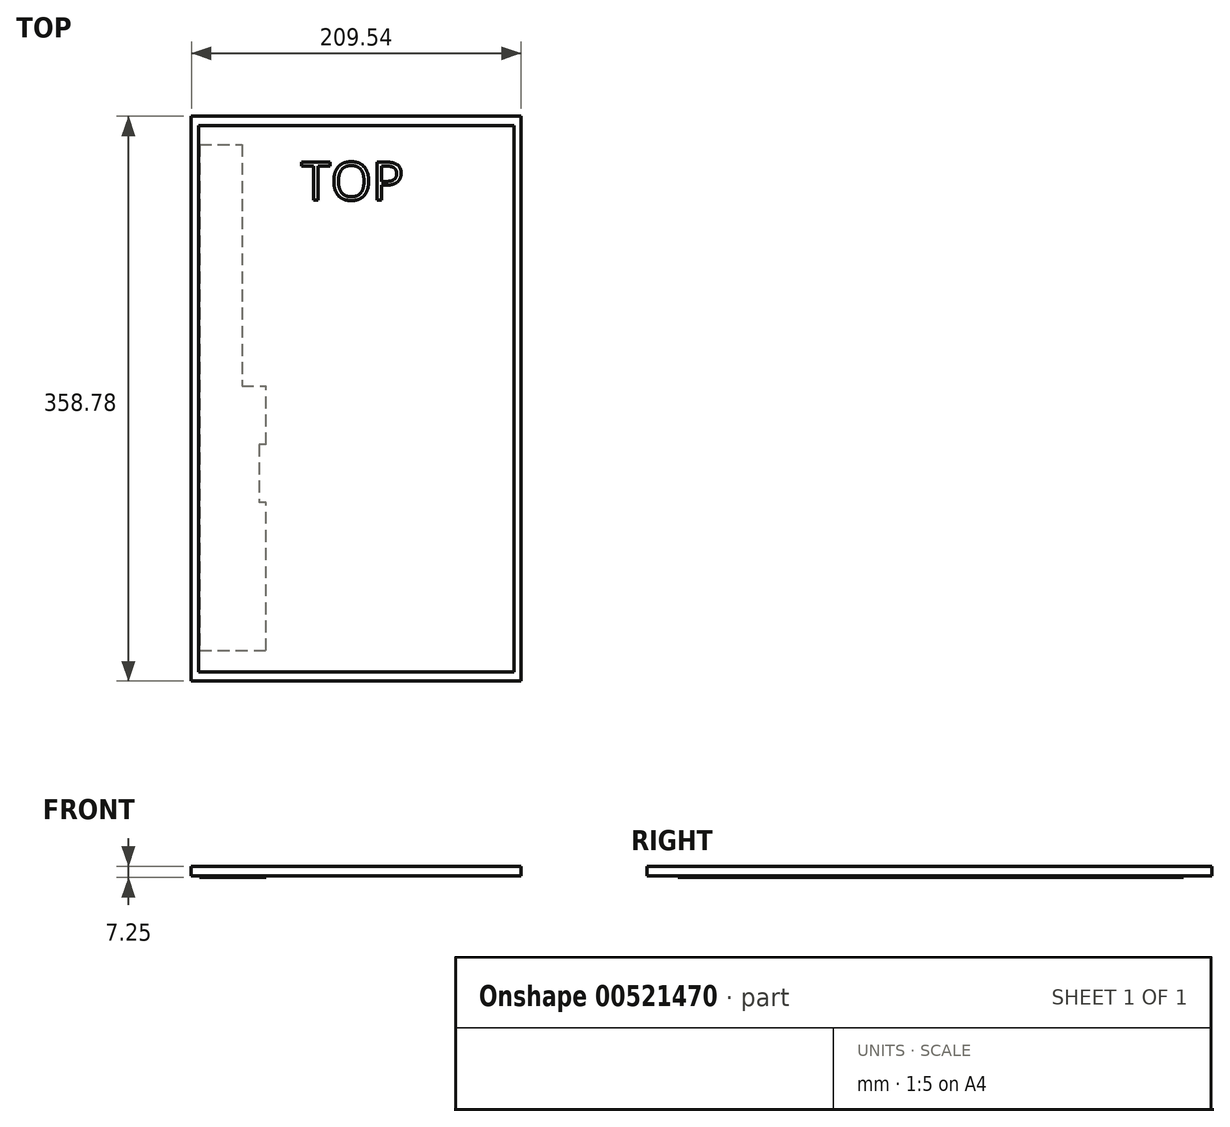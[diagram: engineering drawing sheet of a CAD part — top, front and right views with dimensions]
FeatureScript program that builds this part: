
annotation { "Feature Type Name" : "Feature", "Feature Type Description" : "" }
export const myFeature = defineFeature(function(context is Context, id is Id, definition is map)
    precondition{}
    {
        {
            var Q0;
            Q0=qCreatedBy(makeId("Top.planeOp"),FACE);
            var sketch = newSketch(context, id + "F0", { "sketchPlane" : qUnion([Q0])});
            skLineSegment(sketch, "E0.bottom", {"start": v(-104.77, 179.39) * mm, "end": v(104.78, 179.39) * mm});
            skLineSegment(sketch, "E0.top", {"start": v(-104.78, -179.39) * mm, "end": v(104.77, -179.39) * mm});
            skLineSegment(sketch, "E0.left", {"start": v(-104.77, 179.39) * mm, "end": v(-104.78, -179.39) * mm});
            skLineSegment(sketch, "E0.right", {"start": v(104.78, 179.39) * mm, "end": v(104.77, -179.39) * mm});
            skPoint(sketch, "E0.middle", {"position": v(0, 0) * mm});
            skSolve(sketch);
        }
        {
            var Q0;
            Q0=makeQuery(id+"F0.imprint","IMPRINT",FACE,{"disambiguationData":[TD([[makeQuery(id+"F0.imprint","IMPRINT",EDGE,{"derivedFrom":sQuery(id+"F0.wireOp",EDGE,"E0.bottom")}),-1.0]])]});
            extrude(context, id + "F1", {"entities" : qUnion([Q0]), "depth" : 6 * mm, "offsetDistance" : 25 * mm});
        }
        {
            var Q0;
            Q0=makeQuery(id+"F1.opExtrude","CAP_FACE",FACE,{"disambiguationData":[OSD([sQuery(id+"F0.wireOp",EDGE,"E0.bottom"),sQuery(id+"F0.wireOp",EDGE,"E0.top"),sQuery(id+"F0.wireOp",EDGE,"E0.left"),sQuery(id+"F0.wireOp",EDGE,"E0.right")])],"isStart":false});
            var sketch = newSketch(context, id + "F2", { "sketchPlane" : qUnion([Q0])});
            skLineSegment(sketch, "E1.bottom", {"start": v(-100.08, 173.39) * mm, "end": v(100.08, 173.39) * mm});
            skLineSegment(sketch, "E1.top", {"start": v(-100.08, -173.39) * mm, "end": v(100.08, -173.39) * mm});
            skLineSegment(sketch, "E1.left", {"start": v(-100.08, 173.39) * mm, "end": v(-100.08, -173.39) * mm});
            skLineSegment(sketch, "E1.right", {"start": v(100.08, 173.39) * mm, "end": v(100.08, -173.39) * mm});
            skPoint(sketch, "E1.middle", {"position": v(0, 0) * mm});
            skSolve(sketch);
        }
        {
            var Q0;
            Q0=makeQuery(id+"F2.imprint","IMPRINT",FACE,{"disambiguationData":[TD([[makeQuery(id+"F2.imprint","IMPRINT",EDGE,{"derivedFrom":sQuery(id+"F2.wireOp",EDGE,"E1.bottom")}),-1.0]])]});
            extrude(context, id + "F3", {"entities" : qUnion([Q0]), "operationType" : NewBodyOperationType.REMOVE, "oppositeDirection" : true, "depth" : 0.25 * mm, "offsetDistance" : 25 * mm});
        }
        {
            var Q0;
            Q0=makeQuery(id+"F3.boolean.opBoolean","COPY",FACE,{"derivedFrom":makeQuery(id+"F3.opExtrude","CAP_FACE",FACE,{"disambiguationData":[OSD([sQuery(id+"F2.wireOp",EDGE,"E1.bottom"),sQuery(id+"F2.wireOp",EDGE,"E1.top"),sQuery(id+"F2.wireOp",EDGE,"E1.left"),sQuery(id+"F2.wireOp",EDGE,"E1.right")])],"isStart":false})});
            var sketch = newSketch(context, id + "F4", { "sketchPlane" : qUnion([Q0])});
            skText(sketch, "E2", { "text": "TOP", "fontName": "OpenSans-Regular.ttf"});
            const initialGuessF4  = {"E2": [-0.03496, 0.12616, 1, 0, 0.02427]};
            skSetInitialGuess(sketch, initialGuessF4);
            skSolve(sketch);
        }
        {
            var Q0;
            Q0 = qSketchRegion(id + "F4", true);
            extrude(context, id + "F5", {"entities" : qUnion([Q0]), "operationType" : NewBodyOperationType.ADD, "depth" : 0.5 * mm, "offsetDistance" : 25 * mm});
        }
        {
            var Q0;
            Q0=makeQuery(id+"F1.opExtrude","CAP_FACE",FACE,{"disambiguationData":[OSD([sQuery(id+"F0.wireOp",EDGE,"E0.bottom"),sQuery(id+"F0.wireOp",EDGE,"E0.top"),sQuery(id+"F0.wireOp",EDGE,"E0.left"),sQuery(id+"F0.wireOp",EDGE,"E0.right")])],"isStart":true});
            var sketch = newSketch(context, id + "F6", { "sketchPlane" : qUnion([Q0])});
            skLineSegment(sketch, "E3.bottom", {"start": v(-99.56, -161.28) * mm, "end": v(-72.67, -161.28) * mm});
            skLineSegment(sketch, "E3.top", {"start": v(-99.56, 159.89) * mm, "end": v(-72.67, 159.89) * mm});
            skLineSegment(sketch, "E3.left", {"start": v(-99.56, -161.28) * mm, "end": v(-99.56, 159.89) * mm});
            skLineSegment(sketch, "E3.right", {"start": v(-72.67, -161.28) * mm, "end": v(-72.67, 159.89) * mm});
            skLineSegment(sketch, "E4.bottom", {"start": v(-72.67, 159.89) * mm, "end": v(-57.27, 159.89) * mm});
            skLineSegment(sketch, "E4.top", {"start": v(-72.67, -7.94) * mm, "end": v(-57.27, -7.94) * mm});
            skLineSegment(sketch, "E4.left", {"start": v(-72.67, 159.89) * mm, "end": v(-72.67, -7.94) * mm});
            skLineSegment(sketch, "E4.right", {"start": v(-57.27, 159.89) * mm, "end": v(-57.27, -7.94) * mm});
            skLineSegment(sketch, "E5.bottom", {"start": v(-57.27, 29.06) * mm, "end": v(-61.87, 29.06) * mm});
            skLineSegment(sketch, "E5.top", {"start": v(-57.27, 65.85) * mm, "end": v(-61.87, 65.85) * mm});
            skLineSegment(sketch, "E5.left", {"start": v(-57.27, 29.06) * mm, "end": v(-57.27, 65.85) * mm});
            skLineSegment(sketch, "E5.right", {"start": v(-61.87, 29.06) * mm, "end": v(-61.87, 65.85) * mm});
            skSolve(sketch);
        }
        {
            var Q0;
            {var subQ1=sQuery(id+"F6.wireOp",EDGE,"E4.bottom");Q0=makeQuery(id+"F6.imprint","IMPRINT",FACE,{"disambiguationData":[TD([[makeQuery(id+"F6.imprint","IMPRINT",EDGE,{"derivedFrom":subQ1}),-1.0]])]});}
            var Q1;
            Q1=makeQuery(id+"F6.imprint","IMPRINT",FACE,{"disambiguationData":[TD([[makeQuery(id+"F6.imprint","IMPRINT",EDGE,{"derivedFrom":sQuery(id+"F6.wireOp",EDGE,"E3.bottom")}),1.0]])]});
            extrude(context, id + "F7", {"entities" : qUnion([Q0, Q1]), "operationType" : NewBodyOperationType.ADD, "depth" : 1 * mm, "offsetDistance" : 25 * mm});
        }
    });
